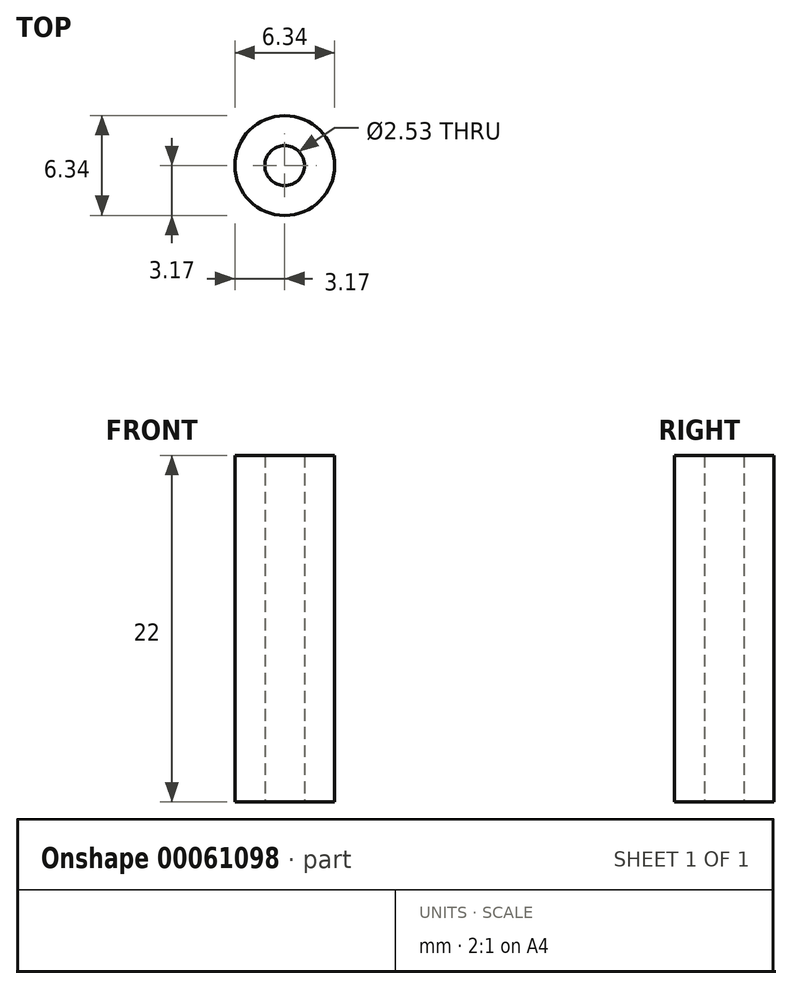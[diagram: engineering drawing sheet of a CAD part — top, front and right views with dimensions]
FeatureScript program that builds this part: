
annotation { "Feature Type Name" : "Feature", "Feature Type Description" : "" }
export const myFeature = defineFeature(function(context is Context, id is Id, definition is map)
    precondition{}
    {
        {
            var Q0;
            Q0=qCreatedBy(makeId("Top.planeOp"),FACE);
            var sketch = newSketch(context, id + "F0", { "sketchPlane" : qUnion([Q0])});
            skCircle(sketch, "E0", {"center": v(0, 0) * mm, "radius": 3.17 * mm});
            skCircle(sketch, "E1", {"center": v(0, 0) * mm, "radius": 1.26 * mm});
            skSolve(sketch);
        }
        {
            var Q0;
            Q0=makeQuery(id+"F0.imprint","IMPRINT",FACE,{"disambiguationData":[TD([[makeQuery(id+"F0.imprint","IMPRINT",EDGE,{"derivedFrom":sQuery(id+"F0.wireOp",EDGE,"E0")}),1.0]])]});
            extrude(context, id + "F1", {"entities" : qUnion([Q0]), "depth" : 22 * mm});
        }
    });
